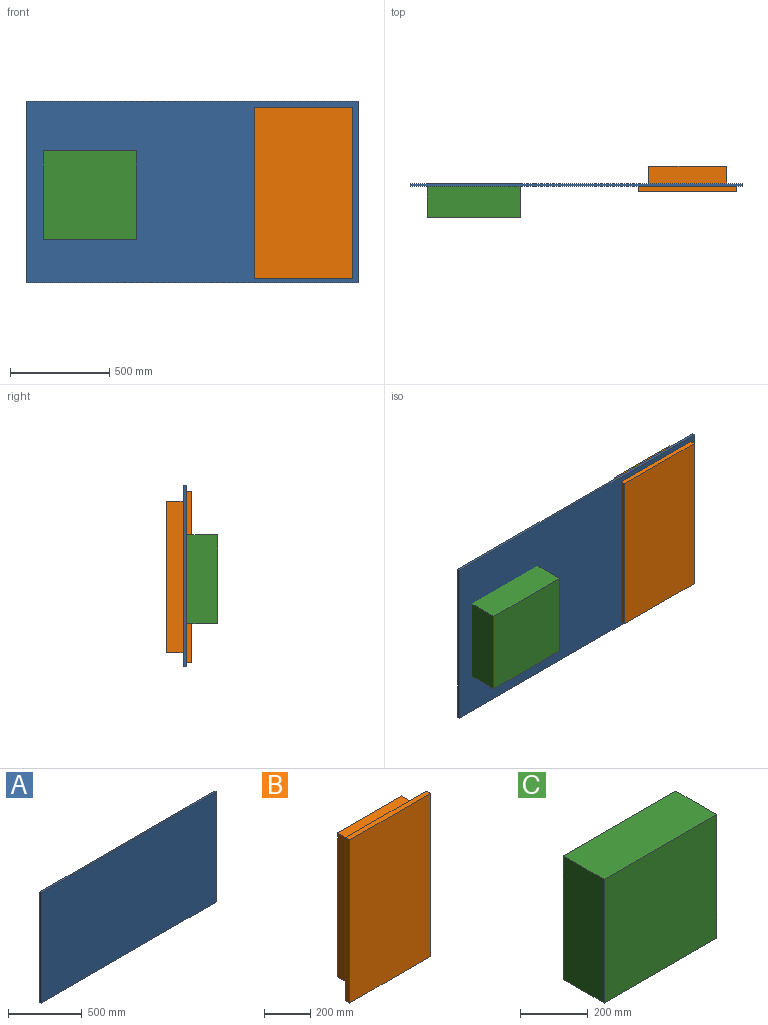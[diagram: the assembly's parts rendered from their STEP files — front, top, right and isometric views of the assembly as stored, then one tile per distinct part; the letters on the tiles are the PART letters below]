
ASSEMBLY  parts=3 mates=2
PART A: 6 faces, bbox 1676.4x12.7x914.4 mm
  f0: plane 1676.4x12.7mm, normal (0,0,-1), area 21290.3mm2, adj f1,f3,f4,f5
  f1: plane 914.4x12.7mm, normal (1,0,0), area 11612.9mm2, adj f0,f2,f4,f5
  f2: plane 1676.4x12.7mm, normal (0,0,1), area 21290.3mm2, adj f1,f3,f4,f5
  f3: plane 914.4x12.7mm, normal (-1,0,0), area 11612.9mm2, adj f0,f2,f4,f5
  f4: plane 1676.4x914.4mm, normal (0,-1,0), area 1532900.2mm2, adj f0,f1,f2,f3
  f5: plane 1676.4x914.4mm, normal (0,1,0), area 1532900.2mm2, adj f0,f1,f2,f3
PART B: 11 faces, bbox 495.3x125.5x866.1 mm
  f0: plane 495.3x25.4mm, normal (0,0,-1), area 12580.6mm2, adj f1,f3,f4,f5
  f1: plane 866.14x25.4mm, normal (1,0,0), area 22000mm2, adj f0,f2,f4,f5
  f2: plane 495.3x25.4mm, normal (0,0,1), area 12580.6mm2, adj f1,f3,f4,f5
  f3: plane 866.14x25.4mm, normal (-1,0,0), area 22000mm2, adj f0,f2,f4,f5
  f4: plane 866.14x495.3mm, normal (0,-1,0), area 428999.1mm2, adj f0,f1,f2,f3
  f5: plane 866.14x495.3mm, normal (0,1,0), area 127999.7mm2, adj f0,f1,f2,f3,f6,f7,f8,f9
  f6: plane 393.7x100.08mm, normal (0,0,-1), area 39399.9mm2, adj f5,f7,f9,f10
  f7: plane 764.54x100.08mm, normal (-1,0,0), area 76512.1mm2, adj f5,f6,f8,f10
  f8: plane 393.7x100.08mm, normal (0,0,1), area 39399.9mm2, adj f5,f7,f9,f10
  f9: plane 764.54x100.08mm, normal (1,0,0), area 76512.1mm2, adj f5,f6,f8,f10
  f10: plane 764.54x393.7mm, normal (0,1,0), area 300999.4mm2, adj f6,f7,f8,f9
PART C: 6 faces, bbox 470.9x170.9x448.1 mm
  f0: plane 470.92x170.94mm, normal (0,0,1), area 80499.3mm2, adj f1,f3,f4,f5
  f1: plane 448.06x170.94mm, normal (-1,0,0), area 76591.6mm2, adj f0,f2,f4,f5
  f2: plane 470.92x170.94mm, normal (0,0,-1), area 80499.3mm2, adj f1,f3,f4,f5
  f3: plane 448.06x170.94mm, normal (1,0,0), area 76591.6mm2, adj f0,f2,f4,f5
  f4: plane 470.92x448.06mm, normal (0,-1,0), area 210996.7mm2, adj f0,f1,f2,f3
  f5: plane 470.92x448.06mm, normal (0,1,0), area 210996.7mm2, adj f0,f1,f2,f3
PLACE A at identity fixed
PLACE B t=(563.61,-12.7,-36.89)mm
PLACE C t=(-751.79,0,-272.89)mm
MATE planar C.f5 <-> A.f5  axis (0,1,0) through (-516.33,0,-48.87)mm
MATE planar B.f5 <-> A.f4  axis (0,1,0) through (366.76,-12.7,345.38)mm
